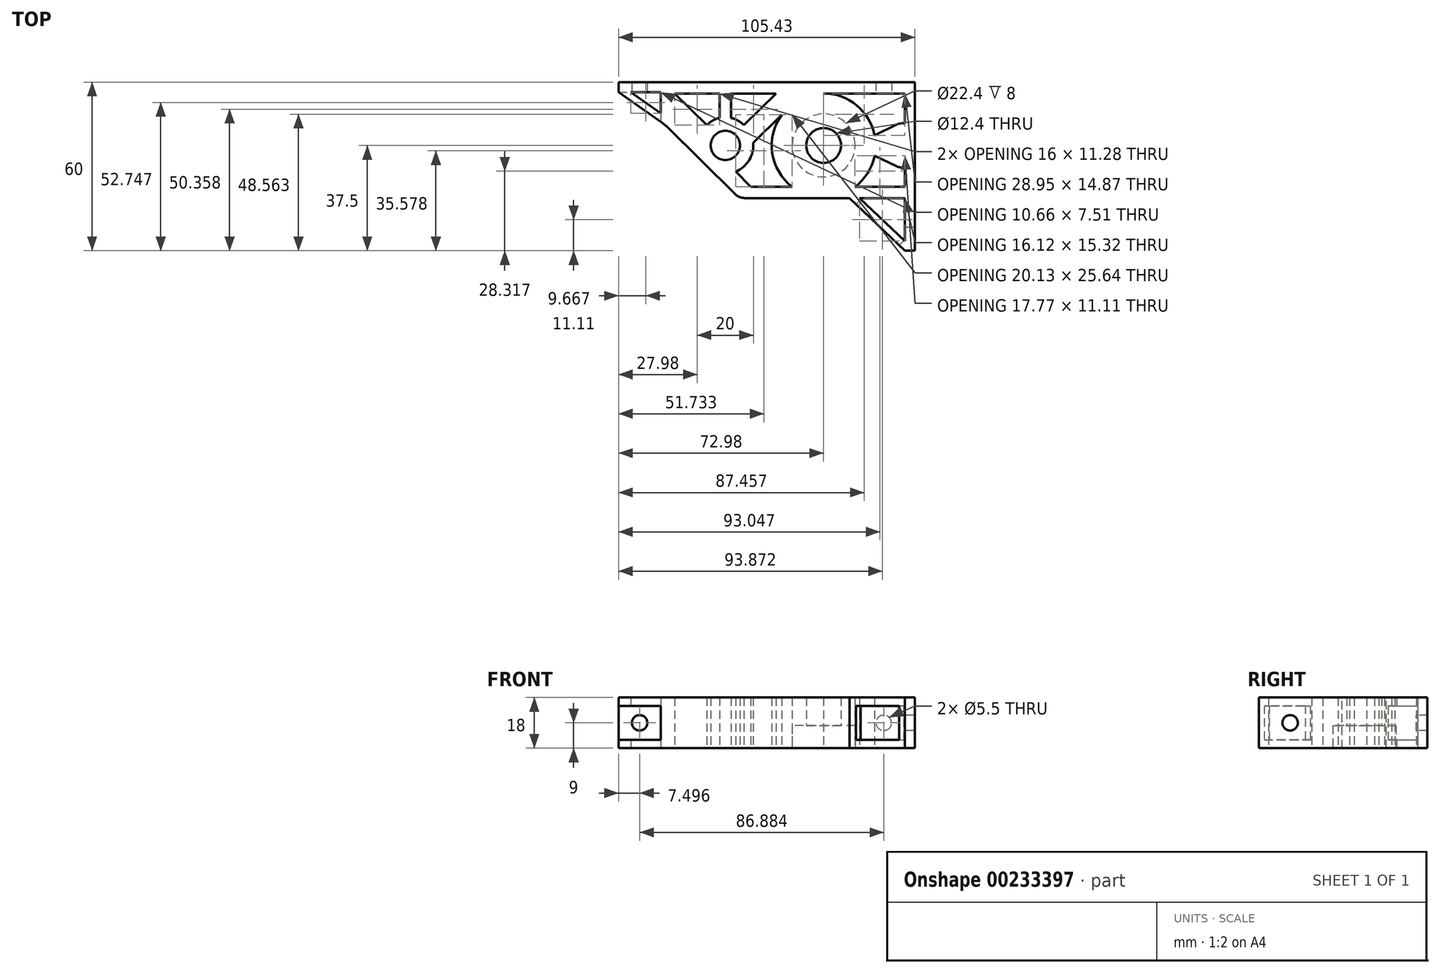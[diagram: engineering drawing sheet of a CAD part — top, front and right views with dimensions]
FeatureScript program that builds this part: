
annotation { "Feature Type Name" : "Feature", "Feature Type Description" : "" }
export const myFeature = defineFeature(function(context is Context, id is Id, definition is map)
    precondition{}
    {
        {
            var Q0;
            Q0=qCreatedBy(makeId("Top.planeOp"),FACE);
            var sketch = newSketch(context, id + "F0", { "sketchPlane" : qUnion([Q0])});
            skLineSegment(sketch, "E0.bottom", {"start": v(-62.55, -10) * mm, "end": v(67.45, -10) * mm, "construction": true});
            skLineSegment(sketch, "E0.top", {"start": v(-62.55, 10) * mm, "end": v(-0.28, 10) * mm, "construction": true});
            skLineSegment(sketch, "E0.left", {"start": v(-62.55, -10) * mm, "end": v(-62.55, 10) * mm, "construction": true});
            skLineSegment(sketch, "E0.right", {"start": v(67.45, -10) * mm, "end": v(67.45, 10) * mm, "construction": true});
            skPoint(sketch, "E0.middle", {"position": v(2.45, 0) * mm});
            skCircle(sketch, "E1", {"center": v(0, 0) * mm, "radius": 5.2 * mm});
            skCircle(sketch, "E2", {"center": v(35, 0) * mm, "radius": 11.2 * mm});
            skLineSegment(sketch, "E3", {"start": v(67.45, 10) * mm, "end": v(60.24, 10) * mm});
            skLineSegment(sketch, "E4", {"start": v(0, 0) * mm, "end": v(0, 22.5) * mm, "construction": true});
            skLineSegment(sketch, "E5", {"start": v(-62.55, 22.5) * mm, "end": v(67.45, 22.5) * mm});
            skLineSegment(sketch, "E6", {"start": v(67.45, 22.5) * mm, "end": v(67.45, -37.5) * mm});
            skLineSegment(sketch, "E7", {"start": v(18, 22.5) * mm, "end": v(18, 18.5) * mm, "construction": true});
            skLineSegment(sketch, "E8", {"start": v(18, 18.5) * mm, "end": v(6.6, 7.22) * mm});
            skLineSegment(sketch, "E9.MirrorCS", {"start": v(-18, 18.5) * mm, "end": v(-6.6, 7.22) * mm});
            skArc(sketch, "E10", {"start": v(6.6, 7.22) * mm, "mid": v(4.49, 8.84) * mm, "end": v(2, 9.78) * mm});
            skLineSegment(sketch, "E11", {"start": v(-2, 9.78) * mm, "end": v(-2, 18.5) * mm});
            skLineSegment(sketch, "E12", {"start": v(-18, 18.5) * mm, "end": v(-2, 18.5) * mm});
            skLineSegment(sketch, "E13.MirrorCS", {"start": v(2, 9.78) * mm, "end": v(2, 18.5) * mm});
            skLineSegment(sketch, "E14.MirrorCS", {"start": v(18, 18.5) * mm, "end": v(2, 18.5) * mm});
            skArc(sketch, "E15.trimOffspring", {"start": v(-2, 9.78) * mm, "mid": v(-4.49, 8.84) * mm, "end": v(-6.6, 7.22) * mm});
            skLineSegment(sketch, "E16.trimOffspring", {"start": v(0.28, 10) * mm, "end": v(67.45, 10) * mm, "construction": true});
            skLineSegment(sketch, "E17", {"start": v(87.45, -37.5) * mm, "end": v(87.45, 42.5) * mm});
            skLineSegment(sketch, "E18", {"start": v(87.45, 42.5) * mm, "end": v(-62.55, 42.5) * mm});
            skLineSegment(sketch, "E19", {"start": v(6.95, -18.73) * mm, "end": v(67.45, -18.73) * mm});
            skLineSegment(sketch, "E20", {"start": v(63.95, -37.5) * mm, "end": v(63.95, 22.5) * mm});
            skLineSegment(sketch, "E21", {"start": v(63.95, -37.5) * mm, "end": v(67.45, -37.5) * mm});
            skLineSegment(sketch, "E22", {"start": v(3.43, -17.28) * mm, "end": v(-21.5, 7.4) * mm});
            skLineSegment(sketch, "E23", {"start": v(-22.98, 10.95) * mm, "end": v(-22.98, 22.5) * mm});
            skLineSegment(sketch, "E24", {"start": v(-22.98, 19) * mm, "end": v(-37.98, 19) * mm});
            skLineSegment(sketch, "E25", {"start": v(-37.98, 19) * mm, "end": v(-37.98, 22.5) * mm});
            skPoint(sketch, "E26.visualSharp", {"position": v(-22.98, 8.86) * mm});
            skArc(sketch, "E26.filletArc", {"start": v(-22.98, 10.95) * mm, "mid": v(-22.6, 9.02) * mm, "end": v(-21.5, 7.4) * mm});
            skPoint(sketch, "E27.visualSharp", {"position": v(4.9, -18.73) * mm});
            skArc(sketch, "E27.filletArc", {"start": v(3.43, -17.28) * mm, "mid": v(5.05, -18.35) * mm, "end": v(6.95, -18.73) * mm});
            skLineSegment(sketch, "E28", {"start": v(63.95, -37.5) * mm, "end": v(44.2, -18.73) * mm});
            skLineSegment(sketch, "E29", {"start": v(47.83, -18.73) * mm, "end": v(63.95, -34.05) * mm});
            skLineSegment(sketch, "E30", {"start": v(-21.5, 7.4) * mm, "end": v(-37.98, 19) * mm});
            skLineSegment(sketch, "E31", {"start": v(-22.98, 11.5) * mm, "end": v(-33.64, 19) * mm});
            skPoint(sketch, "E31.endSnap0", {"position": v(-30.48, 19) * mm});
            skLineSegment(sketch, "E32", {"start": v(9.04, -14.74) * mm, "end": v(23.82, -14.74) * mm});
            skArc(sketch, "E33", {"start": v(-8.02, -5.95) * mm, "mid": v(-7.03, -7.1) * mm, "end": v(-5.87, -8.08) * mm});
            skLineSegment(sketch, "E34", {"start": v(9.04, -14.74) * mm, "end": v(3.69, -9.28) * mm});
            skArc(sketch, "E35.trimOffspring", {"start": v(3.69, -9.28) * mm, "mid": v(8.5, -5.23) * mm, "end": v(9.95, 0.9) * mm});
            skPoint(sketch, "E36.orphan", {"position": v(9.04, 0) * mm});
            skLineSegment(sketch, "E37", {"start": v(53.14, 3.63) * mm, "end": v(61.91, 7.87) * mm});
            skLineSegment(sketch, "E38", {"start": v(61.91, 7.87) * mm, "end": v(61.91, 18.5) * mm});
            skLineSegment(sketch, "E39", {"start": v(61.91, 18.5) * mm, "end": v(35, 18.5) * mm});
            skArc(sketch, "E40", {"start": v(20.05, 10.9) * mm, "mid": v(16.7, -2.7) * mm, "end": v(23.82, -14.74) * mm});
            skLineSegment(sketch, "E41", {"start": v(9.95, 0.9) * mm, "end": v(20.05, 10.9) * mm});
            skLineSegment(sketch, "E42.MirrorCS", {"start": v(53.14, -3.63) * mm, "end": v(61.91, -7.87) * mm});
            skLineSegment(sketch, "E43", {"start": v(61.91, -7.87) * mm, "end": v(61.91, -14.74) * mm});
            skLineSegment(sketch, "E44", {"start": v(61.91, -14.74) * mm, "end": v(46.18, -14.74) * mm});
            skArc(sketch, "E45.trimOffspring", {"start": v(46.18, -14.74) * mm, "mid": v(50.68, -9.82) * mm, "end": v(53.14, -3.63) * mm});
            skArc(sketch, "E46.trimOffspring", {"start": v(53.14, 3.63) * mm, "mid": v(46.73, 14.3) * mm, "end": v(35, 18.5) * mm});
            skSolve(sketch);
        }
        {
            var Q0;
            {var subQ4=sQuery(id+"F0.wireOp",EDGE,"E24");Q0=makeQuery(id+"F0.imprint","IMPRINT",FACE,{"disambiguationData":[TD([[makeQuery(id+"F0.imprint","IMPRINT",EDGE,{"derivedFrom":subQ4}),-1.0]])]});}
            var Q1;
            {var subQ0=sQuery(id+"F0.wireOp",EDGE,"E21");Q1=makeQuery(id+"F0.imprint","IMPRINT",FACE,{"disambiguationData":[TD([[makeQuery(id+"F0.imprint","IMPRINT",EDGE,{"derivedFrom":subQ0}),1.0]])]});}
            var Q2;
            {var subQ0=sQuery(id+"F0.wireOp",EDGE,"E6");var subQ1=sQuery(id+"F0.wireOp",EDGE,"E3");var subQ2=makeQuery(id+"F0.imprint","INTERSECT",VERTEX,{"derivedFrom":[subQ1,subQ0]});Q2=makeQuery(id+"F0.imprint","IMPRINT",FACE,{"disambiguationData":[TD([[makeQuery(id+"F0.imprint","IMPRINT",EDGE,{"disambiguationData":[TD([[subQ2,-1.0]])],"derivedFrom":subQ1}),1.0]])]});}
            var Q3;
            Q3=makeQuery(id+"F0.imprint","IMPRINT",FACE,{"disambiguationData":[TD([[makeQuery(id+"F0.imprint","IMPRINT",EDGE,{"derivedFrom":sQuery(id+"F0.wireOp",EDGE,"E1")}),-1.0]])]});
            var Q4;
            {var subQ0=sQuery(id+"F0.wireOp",EDGE,"E6");var subQ1=sQuery(id+"F0.wireOp",EDGE,"E3");var subQ2=makeQuery(id+"F0.imprint","INTERSECT",VERTEX,{"derivedFrom":[subQ1,subQ0]});Q4=makeQuery(id+"F0.imprint","IMPRINT",FACE,{"disambiguationData":[TD([[makeQuery(id+"F0.imprint","IMPRINT",EDGE,{"disambiguationData":[TD([[subQ2,-1.0]])],"derivedFrom":subQ1}),-1.0]])]});}
            var Q5;
            {var subQ0=sQuery(id+"F0.wireOp",EDGE,"E28");Q5=makeQuery(id+"F0.imprint","IMPRINT",FACE,{"disambiguationData":[TD([[makeQuery(id+"F0.imprint","IMPRINT",EDGE,{"derivedFrom":subQ0}),-1.0]])]});}
            var Q6;
            {var subQ3=sQuery(id+"F0.wireOp",EDGE,"E26.filletArc");Q6=makeQuery(id+"F0.imprint","IMPRINT",FACE,{"disambiguationData":[TD([[makeQuery(id+"F0.imprint","IMPRINT",EDGE,{"derivedFrom":subQ3}),-1.0]])]});}
            extrude(context, id + "F1", {"entities" : qUnion([Q0, Q1, Q2, Q3, Q4, Q5, Q6]), "depth" : 18 * mm});
        }
        {
            var Q0;
            Q0=makeQuery(id+"F1.opExtrude","SWEPT_FACE",FACE,{"disambiguationData":[OSD([sQuery(id+"F0.wireOp",EDGE,"E30")])]});
            var sketch = newSketch(context, id + "F2", { "sketchPlane" : qUnion([Q0])});
            skLineSegment(sketch, "E47", {"start": v(-21.84, 15) * mm, "end": v(-42, 15) * mm});
            skLineSegment(sketch, "E48", {"start": v(-21.84, 3) * mm, "end": v(-42, 3) * mm});
            skSolve(sketch);
        }
        {
            var Q0;
            {var subQ0=sQuery(id+"F2.wireOp",EDGE,"E47");Q0=makeQuery(id+"F2.imprint","IMPRINT",FACE,{"disambiguationData":[TD([[makeQuery(id+"F2.imprint","IMPRINT",EDGE,{"derivedFrom":subQ0}),1.0]])]});}
            var Q1;
            Q1=makeQuery(id+"F1.opExtrude","SWEPT_FACE",FACE,{"disambiguationData":[OSD([sQuery(id+"F0.wireOp",EDGE,"E24")])]});
            extrude(context, id + "F3", {"entities" : qUnion([Q0]), "operationType" : NewBodyOperationType.REMOVE, "endBound" : BoundingType.UP_TO_SURFACE, "oppositeDirection" : true, "endBoundEntityFace" : qUnion([Q1]), "depth" : 25 * mm});
        }
        {
            var Q0;
            {var subQ0=sQuery(id+"F0.wireOp",EDGE,"E30");var subQ1=sQuery(id+"F0.wireOp",EDGE,"E22");Q0=makeQuery(id+"F3.boolean.opBoolean","COPY",FACE,{"disambiguationData":[TD([makeQuery(id+"F1.opExtrude","SWEPT_FACE",FACE,{"disambiguationData":[OSD([sQuery(id+"F0.wireOp",EDGE,"E9.MirrorCS")])]})])],"derivedFrom":makeQuery(id+"F3.opExtrude","SWEPT_FACE",FACE,{"disambiguationData":[OSD([subQ1,sQuery(id+"F0.wireOp",EDGE,"E26.filletArc"),subQ0])]})});}
            var Q1;
            {var subQ0=sQuery(id+"F2.wireOp",EDGE,"E48");var subQ6=sQuery(id+"F0.wireOp",EDGE,"E23");Q1=makeQuery(id+"F3.boolean.opBoolean","SPLIT",FACE,{"disambiguationData":[TD([makeQuery(id+"F3.opExtrude","SWEPT_FACE",FACE,{"disambiguationData":[OSD([subQ0])]})])],"derivedFrom":makeQuery(id+"F1.opExtrude","SWEPT_FACE",FACE,{"disambiguationData":[OSD([subQ6])]})});}
            extrude(context, id + "F4", {"entities" : qUnion([Q0]), "operationType" : NewBodyOperationType.ADD, "endBound" : BoundingType.UP_TO_SURFACE, "endBoundEntityFace" : qUnion([Q1]), "depth" : 25 * mm});
        }
        {
            var Q0;
            {var subQ0=sQuery(id+"F0.wireOp",EDGE,"E30");var subQ1=sQuery(id+"F0.wireOp",EDGE,"E26.filletArc");var subQ2=sQuery(id+"F0.wireOp",EDGE,"E22");var subQ41=makeQuery(id+"F1.opExtrude","SWEPT_EDGE",EDGE,{"disambiguationData":[OSD([subQ2,subQ1,subQ0])]});Q0=makeQuery(id+"F4.boolean.opBoolean","MERGE",EDGE,{"derivedFrom":[makeQuery(id+"F3.boolean.opBoolean","MERGE",EDGE,{"derivedFrom":[subQ41],"fromTools":[makeQuery(id+"F3.opExtrude","CAP_EDGE",EDGE,{"disambiguationData":[OSD([subQ2,subQ1,subQ0])],"isStart":true})]}),makeQuery(id+"F3.boolean.opBoolean","SPLIT",EDGE,{"disambiguationData":[TD([makeQuery(id+"F3.opExtrude","SWEPT_FACE",FACE,{"disambiguationData":[OSD([sQuery(id+"F2.wireOp",EDGE,"E48")])]})])],"derivedFrom":subQ41}),makeQuery(id+"F3.boolean.opBoolean","SPLIT",EDGE,{"disambiguationData":[TD([makeQuery(id+"F3.opExtrude","SWEPT_FACE",FACE,{"disambiguationData":[OSD([sQuery(id+"F2.wireOp",EDGE,"E47")])]})])],"derivedFrom":subQ41}),makeQuery(id+"F4.opExtrude","CAP_EDGE",EDGE,{"disambiguationData":[OSD([subQ2,subQ1,subQ0])],"isStart":true})]});}
            fillet(context, id + "F5", {"entities" : qUnion([Q0]), "radius" : 15 * mm, "tangentPropagation" : true, "allowEdgeOverflow" : false});
        }
        {
            var Q0;
            Q0=makeQuery(id+"F1.opExtrude","SWEPT_FACE",FACE,{"disambiguationData":[OSD([sQuery(id+"F0.wireOp",EDGE,"E28")])]});
            var sketch = newSketch(context, id + "F6", { "sketchPlane" : qUnion([Q0])});
            skLineSegment(sketch, "E49", {"start": v(44.94, 15) * mm, "end": v(72.2, 15) * mm});
            skLineSegment(sketch, "E50", {"start": v(72.2, 3) * mm, "end": v(44.94, 3) * mm});
            skSolve(sketch);
        }
        {
            var Q0;
            {var subQ0=sQuery(id+"F6.wireOp",EDGE,"E49");Q0=makeQuery(id+"F6.imprint","IMPRINT",FACE,{"disambiguationData":[TD([[makeQuery(id+"F6.imprint","IMPRINT",EDGE,{"derivedFrom":subQ0}),-1.0]])]});}
            extrude(context, id + "F7", {"entities" : qUnion([Q0]), "operationType" : NewBodyOperationType.REMOVE, "oppositeDirection" : true, "depth" : 3 * mm});
        }
        {
            var Q0;
            {var subQ0=sQuery(id+"F0.wireOp",EDGE,"E20");var subQ1=sQuery(id+"F6.wireOp",EDGE,"E49");var subQ2=sQuery(id+"F6.wireOp",EDGE,"E50");var subQ3=sQuery(id+"F0.wireOp",EDGE,"E28");var subQ4=sQuery(id+"F0.wireOp",EDGE,"E21");Q0=makeQuery(id+"F7.boolean.opBoolean","COPY",FACE,{"disambiguationData":[TD([makeQuery(id+"F1.opExtrude","SWEPT_FACE",FACE,{"disambiguationData":[OSD([subQ0])]})])],"derivedFrom":makeQuery(id+"F7.opExtrude","CAP_FACE",FACE,{"disambiguationData":[OSD([sQuery(id+"F0.wireOp",EDGE,"E19"),subQ0,subQ4,subQ3,subQ1,subQ2])],"isStart":false})});}
            var Q1;
            {var subQ3=sQuery(id+"F0.wireOp",EDGE,"E28");Q1=makeQuery(id+"F7.boolean.opBoolean","SPLIT",FACE,{"disambiguationData":[TD([makeQuery(id+"F7.opExtrude","SWEPT_FACE",FACE,{"disambiguationData":[OSD([sQuery(id+"F6.wireOp",EDGE,"E50")])]})])],"derivedFrom":makeQuery(id+"F1.opExtrude","SWEPT_FACE",FACE,{"disambiguationData":[OSD([subQ3])]})});}
            extrude(context, id + "F8", {"entities" : qUnion([Q0]), "operationType" : NewBodyOperationType.ADD, "endBound" : BoundingType.UP_TO_SURFACE, "endBoundEntityFace" : qUnion([Q1]), "depth" : 25 * mm});
        }
        {
            var Q0;
            {var subQ0=sQuery(id+"F0.wireOp",EDGE,"E19");var subQ1=sQuery(id+"F0.wireOp",EDGE,"E20");var subQ2=sQuery(id+"F6.wireOp",EDGE,"E49");var subQ3=sQuery(id+"F6.wireOp",EDGE,"E50");var subQ4=sQuery(id+"F0.wireOp",EDGE,"E28");Q0=makeQuery(id+"F7.boolean.opBoolean","COPY",FACE,{"disambiguationData":[TD([makeQuery(id+"F7.opExtrude","SWEPT_FACE",FACE,{"disambiguationData":[OSD([subQ0,subQ4])]})])],"derivedFrom":makeQuery(id+"F7.opExtrude","CAP_FACE",FACE,{"disambiguationData":[OSD([subQ0,subQ1,sQuery(id+"F0.wireOp",EDGE,"E21"),subQ4,subQ2,subQ3])],"isStart":false})});}
            var Q1;
            {var subQ0=sQuery(id+"F6.wireOp",EDGE,"E50");var subQ1=sQuery(id+"F6.wireOp",EDGE,"E49");var subQ2=sQuery(id+"F0.wireOp",EDGE,"E28");var subQ3=sQuery(id+"F0.wireOp",EDGE,"E21");var subQ4=sQuery(id+"F0.wireOp",EDGE,"E20");var subQ5=sQuery(id+"F0.wireOp",EDGE,"E19");var subQ43=makeQuery(id+"F1.opExtrude","SWEPT_FACE",FACE,{"disambiguationData":[OSD([subQ2])]});Q1=makeQuery(id+"F8.boolean.opBoolean","MERGE",FACE,{"derivedFrom":[makeQuery(id+"F7.boolean.opBoolean","SPLIT",FACE,{"disambiguationData":[TD([makeQuery(id+"F7.opExtrude","SWEPT_FACE",FACE,{"disambiguationData":[OSD([subQ0])]})])],"derivedFrom":subQ43}),makeQuery(id+"F7.boolean.opBoolean","SPLIT",FACE,{"disambiguationData":[TD([makeQuery(id+"F7.opExtrude","SWEPT_FACE",FACE,{"disambiguationData":[OSD([subQ1])]})])],"derivedFrom":subQ43}),makeQuery(id+"F8.opExtrude","CAP_FACE",FACE,{"disambiguationData":[OSD([subQ5,subQ4,subQ3,subQ2,subQ1,subQ0])],"isStart":false})]});}
            extrude(context, id + "F9", {"entities" : qUnion([Q0]), "operationType" : NewBodyOperationType.ADD, "endBound" : BoundingType.UP_TO_SURFACE, "endBoundEntityFace" : qUnion([Q1]), "depth" : 25 * mm});
        }
        {
            var Q0;
            Q0=makeQuery(id+"F9.opExtrude","SWEPT_FACE",FACE,{"disambiguationData":[OSD([sQuery(id+"F6.wireOp",EDGE,"E49")])]});
            var Q1;
            Q1=makeQuery(id+"F8.opExtrude","SWEPT_FACE",FACE,{"disambiguationData":[OSD([sQuery(id+"F6.wireOp",EDGE,"E49")])]});
            extrude(context, id + "F10", {"entities" : qUnion([Q0, Q1]), "operationType" : NewBodyOperationType.REMOVE, "oppositeDirection" : true, "depth" : 25 * mm});
        }
        {
            var Q0;
            {var subQ0=sQuery(id+"F0.wireOp",EDGE,"E20");Q0=makeQuery(id+"F10.boolean.opBoolean","MERGE",FACE,{"derivedFrom":[makeQuery(id+"F1.opExtrude","SWEPT_FACE",FACE,{"disambiguationData":[OSD([subQ0])]}),makeQuery(id+"F10.opExtrude","SWEPT_FACE",FACE,{"disambiguationData":[OSD([subQ0,sQuery(id+"F6.wireOp",EDGE,"E49")])]})]});}
            var sketch = newSketch(context, id + "F11", { "sketchPlane" : qUnion([Q0])});
            skLineSegment(sketch, "E51", {"start": v(18.73, 9) * mm, "end": v(34.05, 9) * mm, "construction": true});
            skCircle(sketch, "E52", {"center": v(26.4, 9) * mm, "radius": 2.75 * mm});
            skSolve(sketch);
        }
        {
            var Q0;
            Q0=makeQuery(id+"F11.imprint","IMPRINT",FACE,{"disambiguationData":[TD([[makeQuery(id+"F11.imprint","IMPRINT",EDGE,{"derivedFrom":sQuery(id+"F11.wireOp",EDGE,"E52")}),1.0]])]});
            extrude(context, id + "F12", {"entities" : qUnion([Q0]), "operationType" : NewBodyOperationType.REMOVE, "oppositeDirection" : true, "depth" : 25 * mm});
        }
        {
            var Q0;
            Q0=makeQuery(id+"F1.opExtrude","SWEPT_FACE",FACE,{"disambiguationData":[OSD([sQuery(id+"F0.wireOp",EDGE,"E38")])]});
            var Q1;
            Q1=makeQuery(id+"F1.opExtrude","SWEPT_FACE",FACE,{"disambiguationData":[OSD([sQuery(id+"F0.wireOp",EDGE,"E43")])]});
            var Q2;
            {var subQ0=sQuery(id+"F0.wireOp",EDGE,"E20");Q2=makeQuery(id+"F10.boolean.opBoolean","MERGE",FACE,{"derivedFrom":[makeQuery(id+"F1.opExtrude","SWEPT_FACE",FACE,{"disambiguationData":[OSD([subQ0])]}),makeQuery(id+"F10.opExtrude","SWEPT_FACE",FACE,{"disambiguationData":[OSD([subQ0,sQuery(id+"F6.wireOp",EDGE,"E49")])]})]});}
            extrude(context, id + "F13", {"entities" : qUnion([Q0, Q1]), "operationType" : NewBodyOperationType.REMOVE, "endBound" : BoundingType.UP_TO_SURFACE, "oppositeDirection" : true, "endBoundEntityFace" : qUnion([Q2]), "depth" : 25 * mm});
        }
        {
            var Q0;
            {var subQ0=sQuery(id+"F0.wireOp",EDGE,"E43");var subQ1=sQuery(id+"F0.wireOp",EDGE,"E42.MirrorCS");Q0=makeQuery(id+"F13.boolean.opBoolean","MERGE",EDGE,{"derivedFrom":[makeQuery(id+"F1.opExtrude","SWEPT_EDGE",EDGE,{"disambiguationData":[OSD([subQ1,subQ0])]})],"fromTools":[makeQuery(id+"F13.opExtrude","CAP_EDGE",EDGE,{"disambiguationData":[OSD([subQ1,subQ0])],"isStart":true})]});}
            var Q1;
            {var subQ0=sQuery(id+"F0.wireOp",EDGE,"E38");var subQ1=sQuery(id+"F0.wireOp",EDGE,"E37");Q1=makeQuery(id+"F13.boolean.opBoolean","MERGE",EDGE,{"derivedFrom":[makeQuery(id+"F1.opExtrude","SWEPT_EDGE",EDGE,{"disambiguationData":[OSD([subQ1,subQ0])]})],"fromTools":[makeQuery(id+"F13.opExtrude","CAP_EDGE",EDGE,{"disambiguationData":[OSD([subQ1,subQ0])],"isStart":true})]});}
            fillet(context, id + "F14", {"entities" : qUnion([Q0, Q1]), "radius" : 5 * mm, "tangentPropagation" : true, "allowEdgeOverflow" : false});
        }
        {
            var Q0;
            {var subQ0=sQuery(id+"F2.wireOp",EDGE,"E47");var subQ2=sQuery(id+"F2.wireOp",EDGE,"E48");var subQ4=sQuery(id+"F0.wireOp",EDGE,"E30");var subQ5=sQuery(id+"F0.wireOp",EDGE,"E26.filletArc");var subQ6=sQuery(id+"F0.wireOp",EDGE,"E24");var subQ7=sQuery(id+"F0.wireOp",EDGE,"E22");var subQ8=makeQuery(id+"F3.opExtrude","CAP_FACE",FACE,{"disambiguationData":[OSD([subQ7,subQ6,sQuery(id+"F0.wireOp",EDGE,"E25"),subQ5,subQ4,subQ0,subQ2])],"isStart":false});var subQ9=makeQuery(id+"F1.opExtrude","SWEPT_FACE",FACE,{"disambiguationData":[OSD([subQ6])]});Q0=makeQuery(id+"F4.boolean.opBoolean","SPLIT",FACE,{"disambiguationData":[TD([makeQuery(id+"F4.opExtrude","SWEPT_FACE",FACE,{"disambiguationData":[OSD([sQuery(id+"F0.wireOp",EDGE,"E9.MirrorCS"),subQ7,subQ5,subQ4])]})])],"derivedFrom":makeQuery(id+"F3.boolean.opBoolean","MERGE",FACE,{"derivedFrom":[subQ9],"fromTools":[subQ8]})});}
            var Q1;
            Q1=makeQuery(id+"F1.opExtrude","SWEPT_FACE",FACE,{"disambiguationData":[OSD([sQuery(id+"F0.wireOp",EDGE,"E12")])]});
            extrude(context, id + "F15", {"entities" : qUnion([Q0]), "operationType" : NewBodyOperationType.ADD, "endBound" : BoundingType.UP_TO_SURFACE, "endBoundEntityFace" : qUnion([Q1]), "depth" : 25 * mm});
        }
        {
            var Q0;
            Q0=makeQuery(id+"F4.opExtrude","SWEPT_FACE",FACE,{"disambiguationData":[OSD([sQuery(id+"F0.wireOp",EDGE,"E9.MirrorCS"),sQuery(id+"F0.wireOp",EDGE,"E22"),sQuery(id+"F0.wireOp",EDGE,"E26.filletArc"),sQuery(id+"F0.wireOp",EDGE,"E30")])]});
            var Q1;
            Q1=makeQuery(id+"F1.opExtrude","SWEPT_FACE",FACE,{"disambiguationData":[OSD([sQuery(id+"F0.wireOp",EDGE,"E9.MirrorCS")])]});
            extrude(context, id + "F16", {"entities" : qUnion([Q0]), "operationType" : NewBodyOperationType.ADD, "endBound" : BoundingType.UP_TO_SURFACE, "endBoundEntityFace" : qUnion([Q1]), "depth" : 25 * mm});
        }
        {
            var Q0;
            {var subQ0=sQuery(id+"F0.wireOp",EDGE,"E23");var subQ15=sQuery(id+"F0.wireOp",EDGE,"E30");var subQ19=sQuery(id+"F0.wireOp",EDGE,"E25");var subQ20=sQuery(id+"F0.wireOp",EDGE,"E24");var subQ21=sQuery(id+"F0.wireOp",EDGE,"E22");var subQ37=sQuery(id+"F0.wireOp",EDGE,"E26.filletArc");var subQ38=sQuery(id+"F2.wireOp",EDGE,"E47");var subQ39=sQuery(id+"F2.wireOp",EDGE,"E48");Q0=makeQuery(id+"F4.boolean.opBoolean","SPLIT",FACE,{"disambiguationData":[TD([makeQuery(id+"F1.opExtrude","SWEPT_FACE",FACE,{"disambiguationData":[OSD([subQ0])]})])],"derivedFrom":makeQuery(id+"F3.boolean.opBoolean","MERGE",FACE,{"derivedFrom":[makeQuery(id+"F1.opExtrude","SWEPT_FACE",FACE,{"disambiguationData":[OSD([subQ20])]})],"fromTools":[makeQuery(id+"F3.opExtrude","CAP_FACE",FACE,{"disambiguationData":[OSD([subQ21,subQ20,subQ19,subQ37,subQ15,subQ38,subQ39])],"isStart":false})]})});}
            var sketch = newSketch(context, id + "F17", { "sketchPlane" : qUnion([Q0])});
            skLineSegment(sketch, "E53", {"start": v(-37.98, 9) * mm, "end": v(-22.98, 9) * mm, "construction": true});
            skCircle(sketch, "E54", {"center": v(-30.48, 9) * mm, "radius": 2.75 * mm});
            skSolve(sketch);
        }
        {
            var Q0;
            Q0=makeQuery(id+"F17.imprint","IMPRINT",FACE,{"disambiguationData":[TD([[makeQuery(id+"F17.imprint","IMPRINT",EDGE,{"derivedFrom":sQuery(id+"F17.wireOp",EDGE,"E54")}),1.0]])]});
            extrude(context, id + "F18", {"entities" : qUnion([Q0]), "operationType" : NewBodyOperationType.REMOVE, "oppositeDirection" : true, "depth" : 25 * mm});
        }
        {
            var Q0;
            Q0=makeQuery(id+"F1.opExtrude","CAP_FACE",FACE,{"disambiguationData":[OSD([sQuery(id+"F0.wireOp",EDGE,"E1"),sQuery(id+"F0.wireOp",EDGE,"E2"),sQuery(id+"F0.wireOp",EDGE,"E5"),sQuery(id+"F0.wireOp",EDGE,"E6"),sQuery(id+"F0.wireOp",EDGE,"E8"),sQuery(id+"F0.wireOp",EDGE,"E9.MirrorCS"),sQuery(id+"F0.wireOp",EDGE,"E10"),sQuery(id+"F0.wireOp",EDGE,"E11"),sQuery(id+"F0.wireOp",EDGE,"E12"),sQuery(id+"F0.wireOp",EDGE,"E13.MirrorCS"),sQuery(id+"F0.wireOp",EDGE,"E14.MirrorCS"),sQuery(id+"F0.wireOp",EDGE,"E15.trimOffspring"),sQuery(id+"F0.wireOp",EDGE,"E19"),sQuery(id+"F0.wireOp",EDGE,"E20"),sQuery(id+"F0.wireOp",EDGE,"E21"),sQuery(id+"F0.wireOp",EDGE,"E22"),sQuery(id+"F0.wireOp",EDGE,"E23"),sQuery(id+"F0.wireOp",EDGE,"E24"),sQuery(id+"F0.wireOp",EDGE,"E25"),sQuery(id+"F0.wireOp",EDGE,"E27.filletArc"),sQuery(id+"F0.wireOp",EDGE,"E28"),sQuery(id+"F0.wireOp",EDGE,"E29"),sQuery(id+"F0.wireOp",EDGE,"E30"),sQuery(id+"F0.wireOp",EDGE,"E31"),sQuery(id+"F0.wireOp",EDGE,"E32"),sQuery(id+"F0.wireOp",EDGE,"E34"),sQuery(id+"F0.wireOp",EDGE,"E35.trimOffspring"),sQuery(id+"F0.wireOp",EDGE,"E37"),sQuery(id+"F0.wireOp",EDGE,"E38"),sQuery(id+"F0.wireOp",EDGE,"E39"),sQuery(id+"F0.wireOp",EDGE,"E40"),sQuery(id+"F0.wireOp",EDGE,"E41"),sQuery(id+"F0.wireOp",EDGE,"E42.MirrorCS"),sQuery(id+"F0.wireOp",EDGE,"E43"),sQuery(id+"F0.wireOp",EDGE,"E44"),sQuery(id+"F0.wireOp",EDGE,"E45.trimOffspring"),sQuery(id+"F0.wireOp",EDGE,"E46.trimOffspring")])],"isStart":false});
            var sketch = newSketch(context, id + "F19", { "sketchPlane" : qUnion([Q0])});
            skCircle(sketch, "E55", {"center": v(35, 0) * mm, "radius": 12.71 * mm});
            skSolve(sketch);
        }
        {
            var Q0;
            Q0=makeQuery(id+"F19.imprint","IMPRINT",FACE,{"disambiguationData":[TD([[makeQuery(id+"F19.imprint","IMPRINT",EDGE,{"derivedFrom":makeQuery(id+"F1.opExtrude","CAP_EDGE",EDGE,{"disambiguationData":[OSD([sQuery(id+"F0.wireOp",EDGE,"E2")])],"isStart":false})}),1.0]])]});
            extrude(context, id + "F20", {"entities" : qUnion([Q0]), "operationType" : NewBodyOperationType.ADD, "oppositeDirection" : true, "depth" : 10 * mm});
        }
        {
            var Q0;
            Q0=makeQuery(id+"F20.opExtrude","CAP_FACE",FACE,{"disambiguationData":[OSD([sQuery(id+"F0.wireOp",EDGE,"E2")])],"isStart":false});
            var sketch = newSketch(context, id + "F21", { "sketchPlane" : qUnion([Q0])});
            skCircle(sketch, "E56", {"center": v(35, 0) * mm, "radius": 6.2 * mm});
            skSolve(sketch);
        }
        {
            var Q0;
            Q0=makeQuery(id+"F21.imprint","IMPRINT",FACE,{"disambiguationData":[TD([[makeQuery(id+"F21.imprint","IMPRINT",EDGE,{"derivedFrom":sQuery(id+"F21.wireOp",EDGE,"E56")}),1.0]])]});
            extrude(context, id + "F22", {"entities" : qUnion([Q0]), "operationType" : NewBodyOperationType.REMOVE, "oppositeDirection" : true, "depth" : 25 * mm});
        }
        {
            var Q0;
            {var subQ0=sQuery(id+"F0.wireOp",EDGE,"E39");Q0=makeQuery(id+"F13.boolean.opBoolean","MERGE",FACE,{"derivedFrom":[makeQuery(id+"F1.opExtrude","SWEPT_FACE",FACE,{"disambiguationData":[OSD([subQ0])]})],"fromTools":[makeQuery(id+"F13.opExtrude","SWEPT_FACE",FACE,{"disambiguationData":[OSD([sQuery(id+"F0.wireOp",EDGE,"E38"),subQ0])]})]});}
            var sketch = newSketch(context, id + "F23", { "sketchPlane" : qUnion([Q0])});
            skLineSegment(sketch, "E57", {"start": v(63.95, 9) * mm, "end": v(35, 9) * mm, "construction": true});
            skCircle(sketch, "E58", {"center": v(56.4, 9) * mm, "radius": 2.75 * mm});
            skSolve(sketch);
        }
        {
            var Q0;
            Q0=makeQuery(id+"F23.imprint","IMPRINT",FACE,{"disambiguationData":[TD([[makeQuery(id+"F23.imprint","IMPRINT",EDGE,{"derivedFrom":sQuery(id+"F23.wireOp",EDGE,"E58")}),1.0]])]});
            extrude(context, id + "F24", {"entities" : qUnion([Q0]), "operationType" : NewBodyOperationType.REMOVE, "oppositeDirection" : true, "depth" : 25 * mm});
        }
    });
